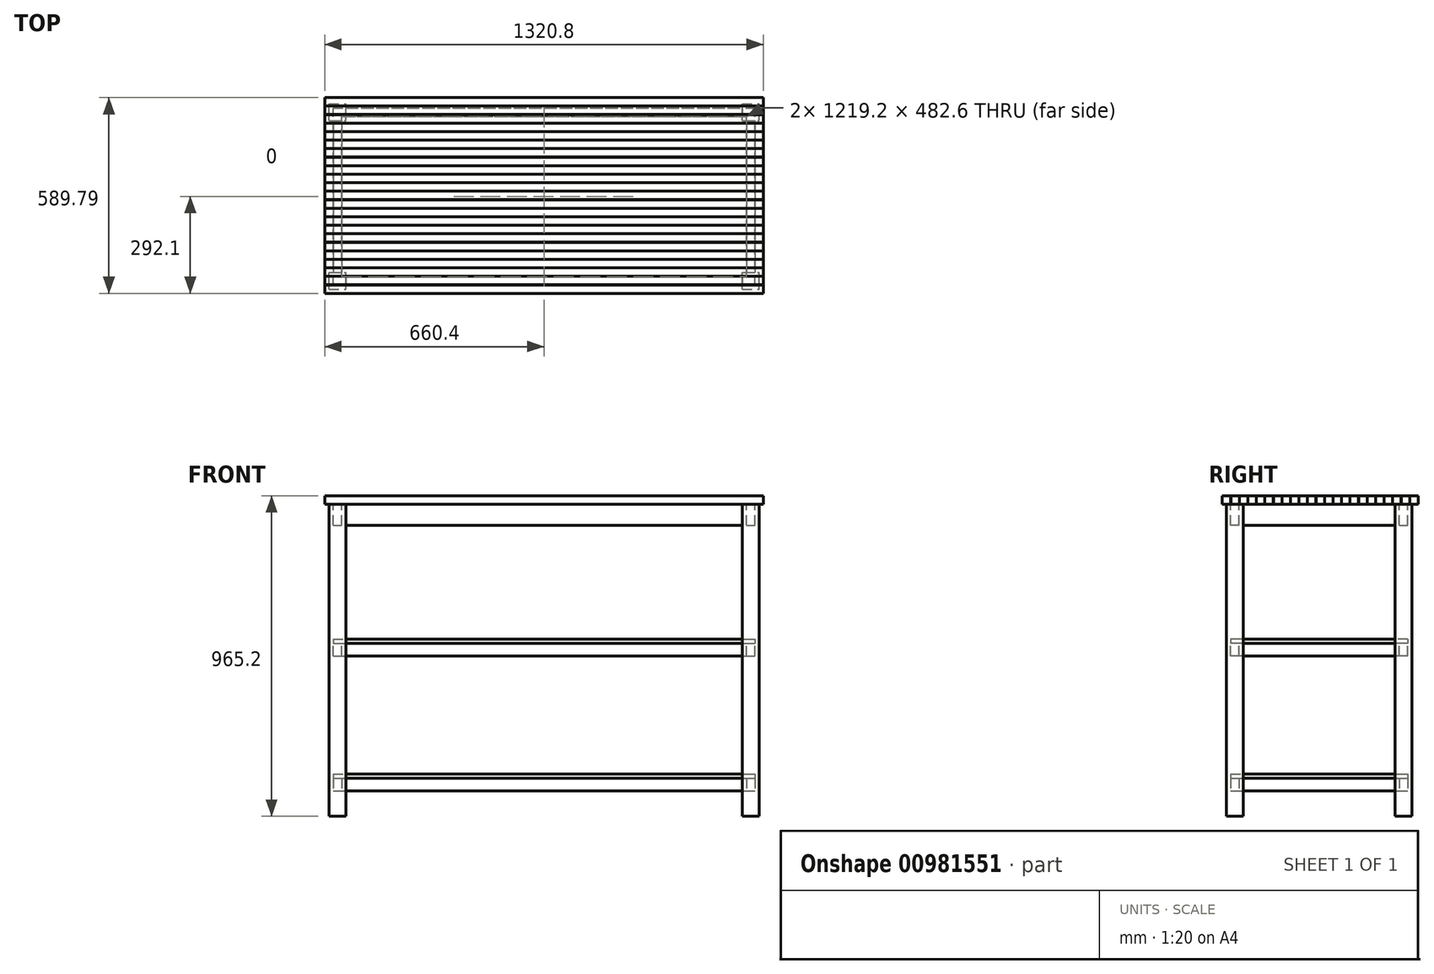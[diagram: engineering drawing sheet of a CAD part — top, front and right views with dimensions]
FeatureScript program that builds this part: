
annotation { "Feature Type Name" : "Feature", "Feature Type Description" : "" }
export const myFeature = defineFeature(function(context is Context, id is Id, definition is map)
    precondition{}
    {
        {
            var Q0;
            Q0=qCreatedBy(makeId("Top.planeOp"),FACE);
            var sketch = newSketch(context, id + "F0", { "sketchPlane" : qUnion([Q0])});
            skLineSegment(sketch, "E0.bottom", {"start": v(0, 0) * mm, "end": v(50.8, 0) * mm});
            skLineSegment(sketch, "E0.top", {"start": v(0, 50.8) * mm, "end": v(50.8, 50.8) * mm});
            skLineSegment(sketch, "E0.left", {"start": v(0, 0) * mm, "end": v(0, 50.8) * mm});
            skLineSegment(sketch, "E0.right", {"start": v(50.8, 0) * mm, "end": v(50.8, 50.8) * mm});
            skLineSegment(sketch, "E1.0.1.0", {"start": v(0, 508) * mm, "end": v(0, 558.8) * mm});
            skLineSegment(sketch, "E1.0.1.1", {"start": v(0, 508) * mm, "end": v(50.8, 508) * mm});
            skLineSegment(sketch, "E1.0.1.2", {"start": v(0, 558.8) * mm, "end": v(50.8, 558.8) * mm});
            skLineSegment(sketch, "E1.0.1.3", {"start": v(50.8, 508) * mm, "end": v(50.8, 558.8) * mm});
            skLineSegment(sketch, "E1.1.0.0", {"start": v(1244.6, 0) * mm, "end": v(1244.6, 50.8) * mm});
            skLineSegment(sketch, "E1.1.0.1", {"start": v(1244.6, 0) * mm, "end": v(1295.4, 0) * mm});
            skLineSegment(sketch, "E1.1.0.2", {"start": v(1244.6, 50.8) * mm, "end": v(1295.4, 50.8) * mm});
            skLineSegment(sketch, "E1.1.0.3", {"start": v(1295.4, 0) * mm, "end": v(1295.4, 50.8) * mm});
            skLineSegment(sketch, "E1.1.1.0", {"start": v(1244.6, 508) * mm, "end": v(1244.6, 558.8) * mm});
            skLineSegment(sketch, "E1.1.1.1", {"start": v(1244.6, 508) * mm, "end": v(1295.4, 508) * mm});
            skLineSegment(sketch, "E1.1.1.2", {"start": v(1244.6, 558.8) * mm, "end": v(1295.4, 558.8) * mm});
            skLineSegment(sketch, "E1.1.1.3", {"start": v(1295.4, 508) * mm, "end": v(1295.4, 558.8) * mm});
            skLineSegment(sketch, "E1.direction1", {"start": v(0, 0) * mm, "end": v(1244.6, 0) * mm, "construction": true});
            skLineSegment(sketch, "E1.direction2", {"start": v(0, 0) * mm, "end": v(0, 508) * mm, "construction": true});
            skSolve(sketch);
        }
        {
            var Q0;
            Q0 = qSketchRegion(id + "F0", true);
            extrude(context, id + "F1", {"entities" : qUnion([Q0]), "depth" : 939.8 * mm, "offsetDistance" : 25.4 * mm});
        }
        {
            var Q0;
            Q0=makeQuery(id+"F1.opExtrude","CAP_FACE",FACE,{"disambiguationData":[OSD([sQuery(id+"F0.wireOp",EDGE,"E1.0.1.0"),sQuery(id+"F0.wireOp",EDGE,"E1.0.1.1"),sQuery(id+"F0.wireOp",EDGE,"E1.0.1.2"),sQuery(id+"F0.wireOp",EDGE,"E1.0.1.3")])],"isStart":false});
            var sketch = newSketch(context, id + "F2", { "sketchPlane" : qUnion([Q0])});
            skLineSegment(sketch, "E2.bottom", {"start": v(50.8, 546.1) * mm, "end": v(1244.6, 546.1) * mm});
            skLineSegment(sketch, "E2.top", {"start": v(50.8, 520.7) * mm, "end": v(1244.6, 520.7) * mm});
            skLineSegment(sketch, "E2.left", {"start": v(50.8, 546.1) * mm, "end": v(50.8, 520.7) * mm});
            skLineSegment(sketch, "E2.right", {"start": v(1244.6, 546.1) * mm, "end": v(1244.6, 520.7) * mm});
            skLineSegment(sketch, "E3.0.1.0", {"start": v(50.8, 12.7) * mm, "end": v(1244.6, 12.7) * mm});
            skLineSegment(sketch, "E3.0.1.1", {"start": v(50.8, 38.1) * mm, "end": v(1244.6, 38.1) * mm});
            skLineSegment(sketch, "E3.direction1", {"start": v(50.8, 520.7) * mm, "end": v(88.9, 520.7) * mm, "construction": true});
            skLineSegment(sketch, "E3.direction2", {"start": v(50.8, 520.7) * mm, "end": v(50.8, 12.7) * mm, "construction": true});
            skLineSegment(sketch, "E4.bottom", {"start": v(12.7, 508) * mm, "end": v(38.1, 508) * mm});
            skLineSegment(sketch, "E4.top", {"start": v(12.7, 50.8) * mm, "end": v(38.1, 50.8) * mm});
            skLineSegment(sketch, "E4.left", {"start": v(12.7, 508) * mm, "end": v(12.7, 50.8) * mm});
            skLineSegment(sketch, "E4.right", {"start": v(38.1, 508) * mm, "end": v(38.1, 50.8) * mm});
            skLineSegment(sketch, "E5.1.0.0", {"start": v(1257.3, 508) * mm, "end": v(1257.3, 50.8) * mm});
            skLineSegment(sketch, "E5.1.0.1", {"start": v(1282.7, 508) * mm, "end": v(1282.7, 50.8) * mm});
            skLineSegment(sketch, "E5.direction1", {"start": v(12.7, 50.8) * mm, "end": v(1257.3, 50.8) * mm, "construction": true});
            skLineSegment(sketch, "E6", {"start": v(1257.3, 508) * mm, "end": v(1282.7, 508) * mm});
            skLineSegment(sketch, "E7", {"start": v(1257.3, 50.8) * mm, "end": v(1282.7, 50.8) * mm});
            skLineSegment(sketch, "E8", {"start": v(50.8, 38.1) * mm, "end": v(50.8, 12.7) * mm});
            skLineSegment(sketch, "E9", {"start": v(1244.6, 38.1) * mm, "end": v(1244.6, 12.7) * mm});
            skSolve(sketch);
        }
        {
            var Q0;
            Q0 = qSketchRegion(id + "F2", true);
            extrude(context, id + "F3", {"entities" : qUnion([Q0]), "oppositeDirection" : true, "depth" : 63.5 * mm, "offsetDistance" : 25.4 * mm});
        }
        {
            var Q0;
            Q0=qCreatedBy(makeId("Top.planeOp"),FACE);
            cPlane(context, id + "F4", {"entities" : qUnion([Q0]), "cplaneType" : CPlaneType.OFFSET, "offset" : 76.2 * mm, "width" : 152.4 * mm, "height" : 152.4 * mm});
        }
        {
            var Q0;
            Q0=qCreatedBy(id+"F4.planeOp",FACE);
            var sketch = newSketch(context, id + "F5", { "sketchPlane" : qUnion([Q0])});
            skLineSegment(sketch, "E10.bottom", {"start": v(12.7, 12.7) * mm, "end": v(1282.7, 12.7) * mm});
            skLineSegment(sketch, "E10.top", {"start": v(12.7, 546.1) * mm, "end": v(1282.7, 546.1) * mm});
            skLineSegment(sketch, "E10.left", {"start": v(12.7, 12.7) * mm, "end": v(12.7, 546.1) * mm});
            skLineSegment(sketch, "E10.right", {"start": v(1282.7, 12.7) * mm, "end": v(1282.7, 546.1) * mm});
            skLineSegment(sketch, "E11.bottom", {"start": v(38.1, 38.1) * mm, "end": v(1257.3, 38.1) * mm});
            skLineSegment(sketch, "E11.top", {"start": v(38.1, 520.7) * mm, "end": v(1257.3, 520.7) * mm});
            skLineSegment(sketch, "E11.left", {"start": v(38.1, 38.1) * mm, "end": v(38.1, 520.7) * mm});
            skLineSegment(sketch, "E11.right", {"start": v(1257.3, 38.1) * mm, "end": v(1257.3, 520.7) * mm});
            skSolve(sketch);
        }
        {
            var Q0;
            Q0 = qSketchRegion(id + "F5", true);
            extrude(context, id + "F6", {"entities" : qUnion([Q0]), "depth" : 38.1 * mm, "offsetDistance" : 25.4 * mm});
        }
        {
            var Q0;
            Q0=makeQuery(id+"F6.opExtrude","CAP_FACE",FACE,{"disambiguationData":[OSD([sQuery(id+"F5.wireOp",EDGE,"E10.bottom"),sQuery(id+"F5.wireOp",EDGE,"E10.top"),sQuery(id+"F5.wireOp",EDGE,"E10.left"),sQuery(id+"F5.wireOp",EDGE,"E10.right"),sQuery(id+"F5.wireOp",EDGE,"E11.bottom"),sQuery(id+"F5.wireOp",EDGE,"E11.top"),sQuery(id+"F5.wireOp",EDGE,"E11.left"),sQuery(id+"F5.wireOp",EDGE,"E11.right")])],"isStart":false});
            var sketch = newSketch(context, id + "F7", { "sketchPlane" : qUnion([Q0])});
            skLineSegment(sketch, "E12.bottom", {"start": v(12.7, 546.1) * mm, "end": v(1282.7, 546.1) * mm});
            skLineSegment(sketch, "E12.top", {"start": v(12.7, 12.7) * mm, "end": v(1282.7, 12.7) * mm});
            skLineSegment(sketch, "E12.left", {"start": v(12.7, 546.1) * mm, "end": v(12.7, 12.7) * mm});
            skLineSegment(sketch, "E12.right", {"start": v(1282.7, 546.1) * mm, "end": v(1282.7, 12.7) * mm});
            skLineSegment(sketch, "E13.direction1", {"start": v(12.7, 12.7) * mm, "end": v(38.1, 12.7) * mm, "construction": true});
            skLineSegment(sketch, "E13.direction2", {"start": v(12.7, 12.7) * mm, "end": v(12.7, 90.17) * mm, "construction": true});
            skSolve(sketch);
        }
        {
            var Q0;
            Q0 = qSketchRegion(id + "F7", true);
            extrude(context, id + "F8", {"entities" : qUnion([Q0]), "depth" : 12.7 * mm, "offsetDistance" : 25.4 * mm});
        }
        {
            var Q0;
            Q0=qCreatedBy(makeId("Top.planeOp"),FACE);
            cPlane(context, id + "F9", {"entities" : qUnion([Q0]), "cplaneType" : CPlaneType.OFFSET, "offset" : 520.7 * mm, "width" : 152.4 * mm, "height" : 152.4 * mm});
        }
        {
            var Q0;
            Q0=qCreatedBy(id+"F9.planeOp",FACE);
            var sketch = newSketch(context, id + "F10", { "sketchPlane" : qUnion([Q0])});
            skLineSegment(sketch, "E14.bottom", {"start": v(12.7, 546.1) * mm, "end": v(1282.7, 546.1) * mm});
            skLineSegment(sketch, "E14.top", {"start": v(12.7, 12.7) * mm, "end": v(1282.7, 12.7) * mm});
            skLineSegment(sketch, "E14.left", {"start": v(12.7, 546.1) * mm, "end": v(12.7, 12.7) * mm});
            skLineSegment(sketch, "E14.right", {"start": v(1282.7, 546.1) * mm, "end": v(1282.7, 12.7) * mm});
            skLineSegment(sketch, "E15.bottom", {"start": v(38.1, 520.7) * mm, "end": v(1257.3, 520.7) * mm});
            skLineSegment(sketch, "E15.top", {"start": v(38.1, 38.1) * mm, "end": v(1257.3, 38.1) * mm});
            skLineSegment(sketch, "E15.left", {"start": v(38.1, 520.7) * mm, "end": v(38.1, 38.1) * mm});
            skLineSegment(sketch, "E15.right", {"start": v(1257.3, 520.7) * mm, "end": v(1257.3, 38.1) * mm});
            skSolve(sketch);
        }
        {
            var Q0;
            Q0 = qSketchRegion(id + "F10", true);
            extrude(context, id + "F11", {"entities" : qUnion([Q0]), "oppositeDirection" : true, "depth" : 38.1 * mm, "offsetDistance" : 25.4 * mm});
        }
        {
            var Q0;
            Q0=makeQuery(id+"F11.opExtrude","CAP_FACE",FACE,{"disambiguationData":[OSD([sQuery(id+"F10.wireOp",EDGE,"E14.bottom"),sQuery(id+"F10.wireOp",EDGE,"E14.top"),sQuery(id+"F10.wireOp",EDGE,"E14.left"),sQuery(id+"F10.wireOp",EDGE,"E14.right"),sQuery(id+"F10.wireOp",EDGE,"E15.bottom"),sQuery(id+"F10.wireOp",EDGE,"E15.top"),sQuery(id+"F10.wireOp",EDGE,"E15.left"),sQuery(id+"F10.wireOp",EDGE,"E15.right")])],"isStart":true});
            var sketch = newSketch(context, id + "F12", { "sketchPlane" : qUnion([Q0])});
            skLineSegment(sketch, "E16.bottom", {"start": v(12.7, 546.1) * mm, "end": v(1282.82, 546.1) * mm});
            skLineSegment(sketch, "E16.top", {"start": v(12.46, 12.7) * mm, "end": v(1282.58, 12.7) * mm});
            skLineSegment(sketch, "E16.left", {"start": v(12.7, 546.1) * mm, "end": v(12.46, 12.7) * mm});
            skLineSegment(sketch, "E16.right", {"start": v(1282.82, 546.1) * mm, "end": v(1282.8, 482.6) * mm});
            skLineSegment(sketch, "E17.direction1", {"start": v(12.7, 546.1) * mm, "end": v(37.87, 546.28) * mm, "construction": true});
            skLineSegment(sketch, "E17.direction2", {"start": v(12.7, 546.1) * mm, "end": v(12.7, 468.63) * mm, "construction": true});
            skSolve(sketch);
        }
        {
            var Q0;
            Q0=makeQuery(id+"F1.opExtrude","CAP_FACE",FACE,{"disambiguationData":[OSD([sQuery(id+"F0.wireOp",EDGE,"E0.bottom"),sQuery(id+"F0.wireOp",EDGE,"E0.top"),sQuery(id+"F0.wireOp",EDGE,"E0.left"),sQuery(id+"F0.wireOp",EDGE,"E0.right")])],"isStart":false});
            var sketch = newSketch(context, id + "F13", { "sketchPlane" : qUnion([Q0])});
            skLineSegment(sketch, "E18.bottom", {"start": v(-12.7, -12.7) * mm, "end": v(1308.1, -12.7) * mm});
            skLineSegment(sketch, "E18.top", {"start": v(-12.7, 12.7) * mm, "end": v(1308.1, 12.7) * mm});
            skLineSegment(sketch, "E18.left", {"start": v(-12.7, -12.7) * mm, "end": v(-12.7, 12.7) * mm});
            skLineSegment(sketch, "E18.right", {"start": v(1308.1, -12.7) * mm, "end": v(1308.1, 12.7) * mm});
            skLineSegment(sketch, "E19.0.1.0", {"start": v(-12.7, 12.95) * mm, "end": v(-12.7, 38.35) * mm});
            skLineSegment(sketch, "E19.0.1.1", {"start": v(-12.7, 38.35) * mm, "end": v(1308.1, 38.35) * mm});
            skLineSegment(sketch, "E19.0.1.2", {"start": v(-12.7, 12.95) * mm, "end": v(1308.1, 12.95) * mm});
            skLineSegment(sketch, "E19.0.1.3", {"start": v(1308.1, 12.95) * mm, "end": v(1308.1, 38.35) * mm});
            skLineSegment(sketch, "E19.0.2.0", {"start": v(-12.7, 38.6) * mm, "end": v(-12.7, 64) * mm});
            skLineSegment(sketch, "E19.0.2.1", {"start": v(-12.7, 64) * mm, "end": v(1308.1, 64) * mm});
            skLineSegment(sketch, "E19.0.2.2", {"start": v(-12.7, 38.6) * mm, "end": v(1308.1, 38.6) * mm});
            skLineSegment(sketch, "E19.0.2.3", {"start": v(1308.1, 38.6) * mm, "end": v(1308.1, 64) * mm});
            skLineSegment(sketch, "E19.0.3.0", {"start": v(-12.7, 64.26) * mm, "end": v(-12.7, 89.66) * mm});
            skLineSegment(sketch, "E19.0.3.1", {"start": v(-12.7, 89.66) * mm, "end": v(1308.1, 89.66) * mm});
            skLineSegment(sketch, "E19.0.3.2", {"start": v(-12.7, 64.26) * mm, "end": v(1308.1, 64.26) * mm});
            skLineSegment(sketch, "E19.0.3.3", {"start": v(1308.1, 64.26) * mm, "end": v(1308.1, 89.66) * mm});
            skLineSegment(sketch, "E19.0.4.0", {"start": v(-12.7, 89.92) * mm, "end": v(-12.7, 115.32) * mm});
            skLineSegment(sketch, "E19.0.4.1", {"start": v(-12.7, 115.32) * mm, "end": v(1308.1, 115.32) * mm});
            skLineSegment(sketch, "E19.0.4.2", {"start": v(-12.7, 89.92) * mm, "end": v(1308.1, 89.92) * mm});
            skLineSegment(sketch, "E19.0.4.3", {"start": v(1308.1, 89.92) * mm, "end": v(1308.1, 115.32) * mm});
            skLineSegment(sketch, "E19.0.5.0", {"start": v(-12.7, 115.57) * mm, "end": v(-12.7, 140.97) * mm});
            skLineSegment(sketch, "E19.0.5.1", {"start": v(-12.7, 140.97) * mm, "end": v(1308.1, 140.97) * mm});
            skLineSegment(sketch, "E19.0.5.2", {"start": v(-12.7, 115.57) * mm, "end": v(1308.1, 115.57) * mm});
            skLineSegment(sketch, "E19.0.5.3", {"start": v(1308.1, 115.57) * mm, "end": v(1308.1, 140.97) * mm});
            skLineSegment(sketch, "E19.0.6.0", {"start": v(-12.7, 141.22) * mm, "end": v(-12.7, 166.62) * mm});
            skLineSegment(sketch, "E19.0.6.1", {"start": v(-12.7, 166.62) * mm, "end": v(1308.1, 166.62) * mm});
            skLineSegment(sketch, "E19.0.6.2", {"start": v(-12.7, 141.22) * mm, "end": v(1308.1, 141.22) * mm});
            skLineSegment(sketch, "E19.0.6.3", {"start": v(1308.1, 141.22) * mm, "end": v(1308.1, 166.62) * mm});
            skLineSegment(sketch, "E19.0.7.0", {"start": v(-12.7, 166.88) * mm, "end": v(-12.7, 192.28) * mm});
            skLineSegment(sketch, "E19.0.7.1", {"start": v(-12.7, 192.28) * mm, "end": v(1308.1, 192.28) * mm});
            skLineSegment(sketch, "E19.0.7.2", {"start": v(-12.7, 166.88) * mm, "end": v(1308.1, 166.88) * mm});
            skLineSegment(sketch, "E19.0.7.3", {"start": v(1308.1, 166.88) * mm, "end": v(1308.1, 192.28) * mm});
            skLineSegment(sketch, "E19.0.8.0", {"start": v(-12.7, 192.53) * mm, "end": v(-12.7, 217.93) * mm});
            skLineSegment(sketch, "E19.0.8.1", {"start": v(-12.7, 217.93) * mm, "end": v(1308.1, 217.93) * mm});
            skLineSegment(sketch, "E19.0.8.2", {"start": v(-12.7, 192.53) * mm, "end": v(1308.1, 192.53) * mm});
            skLineSegment(sketch, "E19.0.8.3", {"start": v(1308.1, 192.53) * mm, "end": v(1308.1, 217.93) * mm});
            skLineSegment(sketch, "E19.0.9.0", {"start": v(-12.7, 218.19) * mm, "end": v(-12.7, 243.59) * mm});
            skLineSegment(sketch, "E19.0.9.1", {"start": v(-12.7, 243.59) * mm, "end": v(1308.1, 243.59) * mm});
            skLineSegment(sketch, "E19.0.9.2", {"start": v(-12.7, 218.19) * mm, "end": v(1308.1, 218.19) * mm});
            skLineSegment(sketch, "E19.0.9.3", {"start": v(1308.1, 218.19) * mm, "end": v(1308.1, 243.59) * mm});
            skLineSegment(sketch, "E19.0.10.0", {"start": v(-12.7, 243.84) * mm, "end": v(-12.7, 269.24) * mm});
            skLineSegment(sketch, "E19.0.10.1", {"start": v(-12.7, 269.24) * mm, "end": v(1308.1, 269.24) * mm});
            skLineSegment(sketch, "E19.0.10.2", {"start": v(-12.7, 243.84) * mm, "end": v(1308.1, 243.84) * mm});
            skLineSegment(sketch, "E19.0.10.3", {"start": v(1308.1, 243.84) * mm, "end": v(1308.1, 269.24) * mm});
            skLineSegment(sketch, "E19.0.11.0", {"start": v(-12.7, 269.5) * mm, "end": v(-12.7, 294.9) * mm});
            skLineSegment(sketch, "E19.0.11.1", {"start": v(-12.7, 294.9) * mm, "end": v(1308.1, 294.9) * mm});
            skLineSegment(sketch, "E19.0.11.2", {"start": v(-12.7, 269.5) * mm, "end": v(1308.1, 269.5) * mm});
            skLineSegment(sketch, "E19.0.11.3", {"start": v(1308.1, 269.5) * mm, "end": v(1308.1, 294.9) * mm});
            skLineSegment(sketch, "E19.0.12.0", {"start": v(-12.7, 295.15) * mm, "end": v(-12.7, 320.55) * mm});
            skLineSegment(sketch, "E19.0.12.1", {"start": v(-12.7, 320.55) * mm, "end": v(1308.1, 320.55) * mm});
            skLineSegment(sketch, "E19.0.12.2", {"start": v(-12.7, 295.15) * mm, "end": v(1308.1, 295.15) * mm});
            skLineSegment(sketch, "E19.0.12.3", {"start": v(1308.1, 295.15) * mm, "end": v(1308.1, 320.55) * mm});
            skLineSegment(sketch, "E19.0.13.0", {"start": v(-12.7, 320.8) * mm, "end": v(-12.7, 346.2) * mm});
            skLineSegment(sketch, "E19.0.13.1", {"start": v(-12.7, 346.2) * mm, "end": v(1308.1, 346.2) * mm});
            skLineSegment(sketch, "E19.0.13.2", {"start": v(-12.7, 320.8) * mm, "end": v(1308.1, 320.8) * mm});
            skLineSegment(sketch, "E19.0.13.3", {"start": v(1308.1, 320.8) * mm, "end": v(1308.1, 346.2) * mm});
            skLineSegment(sketch, "E19.0.14.0", {"start": v(-12.7, 346.46) * mm, "end": v(-12.7, 371.86) * mm});
            skLineSegment(sketch, "E19.0.14.1", {"start": v(-12.7, 371.86) * mm, "end": v(1308.1, 371.86) * mm});
            skLineSegment(sketch, "E19.0.14.2", {"start": v(-12.7, 346.46) * mm, "end": v(1308.1, 346.46) * mm});
            skLineSegment(sketch, "E19.0.14.3", {"start": v(1308.1, 346.46) * mm, "end": v(1308.1, 371.86) * mm});
            skLineSegment(sketch, "E19.0.15.0", {"start": v(-12.7, 372.1) * mm, "end": v(-12.7, 397.51) * mm});
            skLineSegment(sketch, "E19.0.15.1", {"start": v(-12.7, 397.51) * mm, "end": v(1308.1, 397.51) * mm});
            skLineSegment(sketch, "E19.0.15.2", {"start": v(-12.7, 372.11) * mm, "end": v(1308.1, 372.11) * mm});
            skLineSegment(sketch, "E19.0.15.3", {"start": v(1308.1, 372.11) * mm, "end": v(1308.1, 397.51) * mm});
            skLineSegment(sketch, "E19.0.16.0", {"start": v(-12.7, 397.76) * mm, "end": v(-12.7, 423.16) * mm});
            skLineSegment(sketch, "E19.0.16.1", {"start": v(-12.7, 423.16) * mm, "end": v(1308.1, 423.16) * mm});
            skLineSegment(sketch, "E19.0.16.2", {"start": v(-12.7, 397.76) * mm, "end": v(1308.1, 397.76) * mm});
            skLineSegment(sketch, "E19.0.16.3", {"start": v(1308.1, 397.76) * mm, "end": v(1308.1, 423.16) * mm});
            skLineSegment(sketch, "E19.0.17.0", {"start": v(-12.7, 423.42) * mm, "end": v(-12.7, 448.82) * mm});
            skLineSegment(sketch, "E19.0.17.1", {"start": v(-12.7, 448.82) * mm, "end": v(1308.1, 448.82) * mm});
            skLineSegment(sketch, "E19.0.17.2", {"start": v(-12.7, 423.42) * mm, "end": v(1308.1, 423.42) * mm});
            skLineSegment(sketch, "E19.0.17.3", {"start": v(1308.1, 423.42) * mm, "end": v(1308.1, 448.82) * mm});
            skLineSegment(sketch, "E19.0.18.0", {"start": v(-12.7, 449.07) * mm, "end": v(-12.7, 474.47) * mm});
            skLineSegment(sketch, "E19.0.18.1", {"start": v(-12.7, 474.47) * mm, "end": v(1308.1, 474.47) * mm});
            skLineSegment(sketch, "E19.0.18.2", {"start": v(-12.7, 449.07) * mm, "end": v(1308.1, 449.07) * mm});
            skLineSegment(sketch, "E19.0.18.3", {"start": v(1308.1, 449.07) * mm, "end": v(1308.1, 474.47) * mm});
            skLineSegment(sketch, "E19.0.19.0", {"start": v(-12.7, 474.73) * mm, "end": v(-12.7, 500.13) * mm});
            skLineSegment(sketch, "E19.0.19.1", {"start": v(-12.7, 500.13) * mm, "end": v(1308.1, 500.13) * mm});
            skLineSegment(sketch, "E19.0.19.2", {"start": v(-12.7, 474.73) * mm, "end": v(1308.1, 474.73) * mm});
            skLineSegment(sketch, "E19.0.19.3", {"start": v(1308.1, 474.73) * mm, "end": v(1308.1, 500.13) * mm});
            skLineSegment(sketch, "E19.0.20.0", {"start": v(-12.7, 500.38) * mm, "end": v(-12.7, 525.78) * mm});
            skLineSegment(sketch, "E19.0.20.1", {"start": v(-12.7, 525.78) * mm, "end": v(1308.1, 525.78) * mm});
            skLineSegment(sketch, "E19.0.20.2", {"start": v(-12.7, 500.38) * mm, "end": v(1308.1, 500.38) * mm});
            skLineSegment(sketch, "E19.0.20.3", {"start": v(1308.1, 500.38) * mm, "end": v(1308.1, 525.78) * mm});
            skLineSegment(sketch, "E19.0.21.0", {"start": v(-12.7, 526.03) * mm, "end": v(-12.7, 551.43) * mm});
            skLineSegment(sketch, "E19.0.21.1", {"start": v(-12.7, 551.43) * mm, "end": v(1308.1, 551.43) * mm});
            skLineSegment(sketch, "E19.0.21.2", {"start": v(-12.7, 526.03) * mm, "end": v(1308.1, 526.03) * mm});
            skLineSegment(sketch, "E19.0.21.3", {"start": v(1308.1, 526.03) * mm, "end": v(1308.1, 551.43) * mm});
            skLineSegment(sketch, "E19.0.22.0", {"start": v(-12.7, 551.69) * mm, "end": v(-12.7, 577.09) * mm});
            skLineSegment(sketch, "E19.0.22.1", {"start": v(-12.7, 577.09) * mm, "end": v(1308.1, 577.09) * mm});
            skLineSegment(sketch, "E19.0.22.2", {"start": v(-12.7, 551.69) * mm, "end": v(1308.1, 551.69) * mm});
            skLineSegment(sketch, "E19.0.22.3", {"start": v(1308.1, 551.69) * mm, "end": v(1308.1, 577.09) * mm});
            skLineSegment(sketch, "E19.direction1", {"start": v(-12.7, -12.7) * mm, "end": v(12.7, -12.7) * mm, "construction": true});
            skLineSegment(sketch, "E19.direction2", {"start": v(-12.7, -12.7) * mm, "end": v(-12.7, 12.95) * mm, "construction": true});
            skSolve(sketch);
        }
        {
            var Q0;
            Q0 = qSketchRegion(id + "F13", true);
            extrude(context, id + "F14", {"entities" : qUnion([Q0]), "depth" : 25.4 * mm, "offsetDistance" : 25.4 * mm});
        }
        {
            var Q0;
            Q0 = qSketchRegion(id + "F12", true);
            var Q1;
            Q1=makeQuery(id+"F12.imprint","IMPRINT",FACE,{"disambiguationData":[TD([[makeQuery(id+"F12.imprint","IMPRINT",EDGE,{"derivedFrom":makeQuery(id+"F11.opExtrude","CAP_EDGE",EDGE,{"disambiguationData":[OSD([sQuery(id+"F10.wireOp",EDGE,"E15.bottom")])],"isStart":true})}),-1.0]])]});
            var Q2;
            {var subQ0=makeQuery(id+"F11.opExtrude","CAP_EDGE",EDGE,{"disambiguationData":[OSD([sQuery(id+"F10.wireOp",EDGE,"E14.left")])],"isStart":true});Q2=makeQuery(id+"F12.imprint","IMPRINT",FACE,{"disambiguationData":[TD([[makeQuery(id+"F12.imprint","IMPRINT",EDGE,{"derivedFrom":subQ0}),1.0]])]});}
            extrude(context, id + "F15", {"entities" : qUnion([Q0, Q1, Q2]), "depth" : 12.7 * mm, "offsetDistance" : 25.4 * mm});
        }
    });
